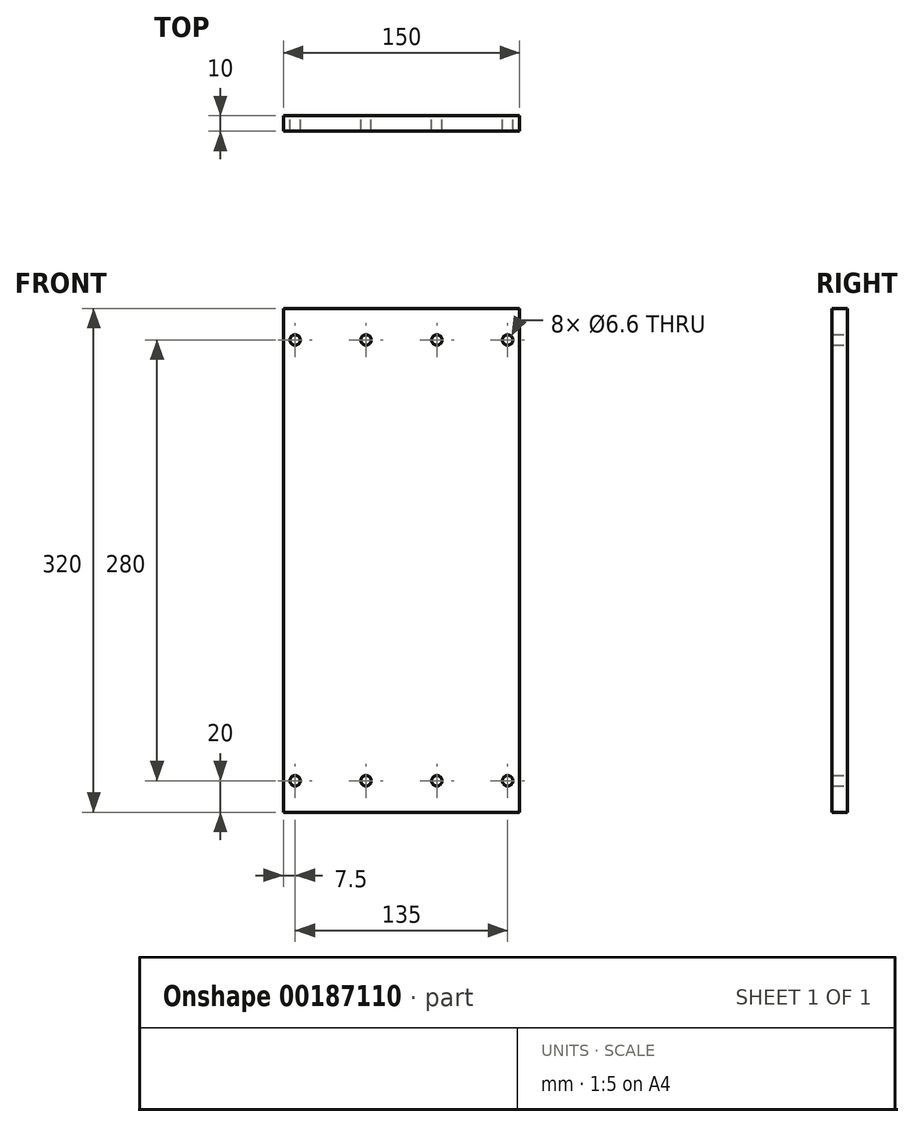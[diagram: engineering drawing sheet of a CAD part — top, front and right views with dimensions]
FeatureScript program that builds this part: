
annotation { "Feature Type Name" : "Feature", "Feature Type Description" : "" }
export const myFeature = defineFeature(function(context is Context, id is Id, definition is map)
    precondition{}
    {
        {
            var Q0;
            Q0=qCreatedBy(makeId("Front.planeOp"),FACE);
            var sketch = newSketch(context, id + "F0", { "sketchPlane" : qUnion([Q0])});
            skLineSegment(sketch, "E0.bottom", {"start": v(75, -160) * mm, "end": v(-75, -160) * mm});
            skLineSegment(sketch, "E0.top", {"start": v(75, 160) * mm, "end": v(-75, 160) * mm});
            skLineSegment(sketch, "E0.left", {"start": v(75, -160) * mm, "end": v(75, 160) * mm});
            skLineSegment(sketch, "E0.right", {"start": v(-75, -160) * mm, "end": v(-75, 160) * mm});
            skPoint(sketch, "E0.middle", {"position": v(0, 0) * mm});
            skCircle(sketch, "E1", {"center": v(-67.5, 140) * mm, "radius": 3.3 * mm});
            skCircle(sketch, "E2", {"center": v(-22.5, 140) * mm, "radius": 3.3 * mm});
            skCircle(sketch, "E3", {"center": v(22.5, 140) * mm, "radius": 3.3 * mm});
            skCircle(sketch, "E4", {"center": v(67.5, 140) * mm, "radius": 3.3 * mm});
            skCircle(sketch, "E5", {"center": v(-67.5, -140) * mm, "radius": 3.3 * mm});
            skCircle(sketch, "E6", {"center": v(-22.5, -140) * mm, "radius": 3.3 * mm});
            skCircle(sketch, "E7", {"center": v(22.5, -140) * mm, "radius": 3.3 * mm});
            skCircle(sketch, "E8", {"center": v(67.5, -140) * mm, "radius": 3.3 * mm});
            skSolve(sketch);
        }
        {
            var Q0;
            Q0=makeQuery(id+"F0.imprint","IMPRINT",FACE,{"disambiguationData":[TD([[makeQuery(id+"F0.imprint","IMPRINT",EDGE,{"derivedFrom":sQuery(id+"F0.wireOp",EDGE,"E0.bottom")}),-1.0]])]});
            extrude(context, id + "F1", {"entities" : qUnion([Q0]), "depth" : 10 * mm});
        }
    });
